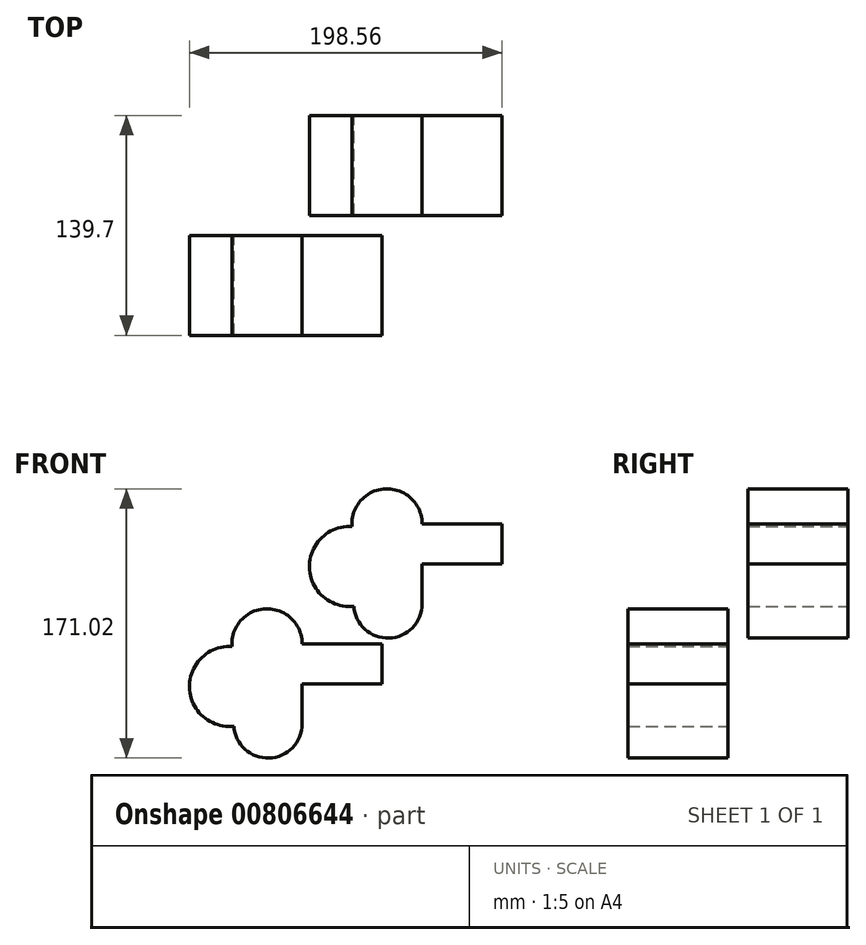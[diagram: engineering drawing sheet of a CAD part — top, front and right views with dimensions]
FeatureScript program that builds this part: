
annotation { "Feature Type Name" : "Feature", "Feature Type Description" : "" }
export const myFeature = defineFeature(function(context is Context, id is Id, definition is map)
    precondition{}
    {
        {
            var Q0;
            Q0=qCreatedBy(makeId("Front.planeOp"),FACE);
            var sketch = newSketch(context, id + "F0", { "sketchPlane" : qUnion([Q0])});
            skLineSegment(sketch, "E0.bottom", {"start": v(-25.4, 25.4) * mm, "end": v(25.4, 25.4) * mm});
            skLineSegment(sketch, "E0.top", {"start": v(-25.4, -25.4) * mm, "end": v(25.4, -25.4) * mm});
            skLineSegment(sketch, "E0.left", {"start": v(-25.4, 25.4) * mm, "end": v(-25.4, -25.4) * mm});
            skLineSegment(sketch, "E0.right", {"start": v(25.4, 25.4) * mm, "end": v(25.4, -25.4) * mm});
            skPoint(sketch, "E0.middle", {"position": v(0, 0) * mm});
            skCircle(sketch, "E1", {"center": v(-71.56, -1.61) * mm, "radius": 25.4 * mm});
            skArc(sketch, "E2", {"start": v(-25.4, 25.4) * mm, "mid": v(-48.54, 47.7) * mm, "end": v(-69.95, 23.74) * mm});
            skArc(sketch, "E3", {"start": v(-68.77, -26.86) * mm, "mid": v(-46.38, -47.1) * mm, "end": v(-25.4, -25.4) * mm});
            skSolve(sketch);
        }
        {
            var Q0;
            Q0=makeQuery(id+"F0.imprint","IMPRINT",FACE,{"disambiguationData":[TD([[makeQuery(id+"F0.imprint","IMPRINT",EDGE,{"derivedFrom":sQuery(id+"F0.wireOp",EDGE,"E0.left")}),-1.0]])]});
            var Q1;
            {var subQ0=sQuery(id+"F0.wireOp",EDGE,"E1");var subQ1=makeQuery(id+"F0.imprint","INTERSECT",VERTEX,{"derivedFrom":[subQ0,sQuery(id+"F0.wireOp",EDGE,"E2")]});Q1=makeQuery(id+"F0.imprint","IMPRINT",FACE,{"disambiguationData":[TD([[makeQuery(id+"F0.imprint","IMPRINT",EDGE,{"disambiguationData":[TD([[subQ1,-1.0]])],"derivedFrom":subQ0}),1.0]])]});}
            var Q2;
            Q2=makeQuery(id+"F0.imprint","IMPRINT",FACE,{"disambiguationData":[TD([[makeQuery(id+"F0.imprint","IMPRINT",EDGE,{"derivedFrom":sQuery(id+"F0.wireOp",EDGE,"E0.bottom")}),-1.0]])]});
            extrude(context, id + "F1", {"entities" : qUnion([Q0, Q1, Q2]), "endBound" : BoundingType.SYMMETRIC, "depth" : 101.6 * mm, "offsetDistance" : 25.4 * mm});
        }
        {
            var Q0;
            Q0=makeQuery(id+"F1.opExtrude","CAP_FACE",FACE,{"disambiguationData":[OSD([sQuery(id+"F0.wireOp",EDGE,"E0.bottom"),sQuery(id+"F0.wireOp",EDGE,"E0.top"),sQuery(id+"F0.wireOp",EDGE,"E0.right"),sQuery(id+"F0.wireOp",EDGE,"E1"),sQuery(id+"F0.wireOp",EDGE,"E2"),sQuery(id+"F0.wireOp",EDGE,"E3")])],"isStart":false});
            extrude(context, id + "F2", {"entities" : qUnion([Q0]), "operationType" : NewBodyOperationType.REMOVE, "endBound" : BoundingType.SYMMETRIC, "depth" : 76.2 * mm, "offsetDistance" : 25.4 * mm});
        }
        {
            var Q0;
            Q0=makeQuery(id+"F1.opExtrude","SWEPT_FACE",FACE,{"disambiguationData":[OSD([sQuery(id+"F0.wireOp",EDGE,"E0.top")])]});
            extrude(context, id + "F3", {"entities" : qUnion([Q0]), "operationType" : NewBodyOperationType.REMOVE, "oppositeDirection" : true, "depth" : 25.4 * mm, "offsetDistance" : 25.4 * mm});
        }
        {
            var Q0;
            Q0=makeQuery(id+"F1.opExtrude","SWEPT_BODY",BODY,{"disambiguationData":[OSD([sQuery(id+"F0.wireOp",EDGE,"E0.bottom"),sQuery(id+"F0.wireOp",EDGE,"E0.top"),sQuery(id+"F0.wireOp",EDGE,"E0.right"),sQuery(id+"F0.wireOp",EDGE,"E1"),sQuery(id+"F0.wireOp",EDGE,"E2"),sQuery(id+"F0.wireOp",EDGE,"E3")])]});
            transform(context, id + "F4", {"entities" : qUnion([Q0]), "transformType" : TransformType.TRANSLATION_3D, "dx" : 76.2 * mm, "dy" : 76.2 * mm, "dz" : 76.2 * mm, "makeCopy" : true});
        }
    });
